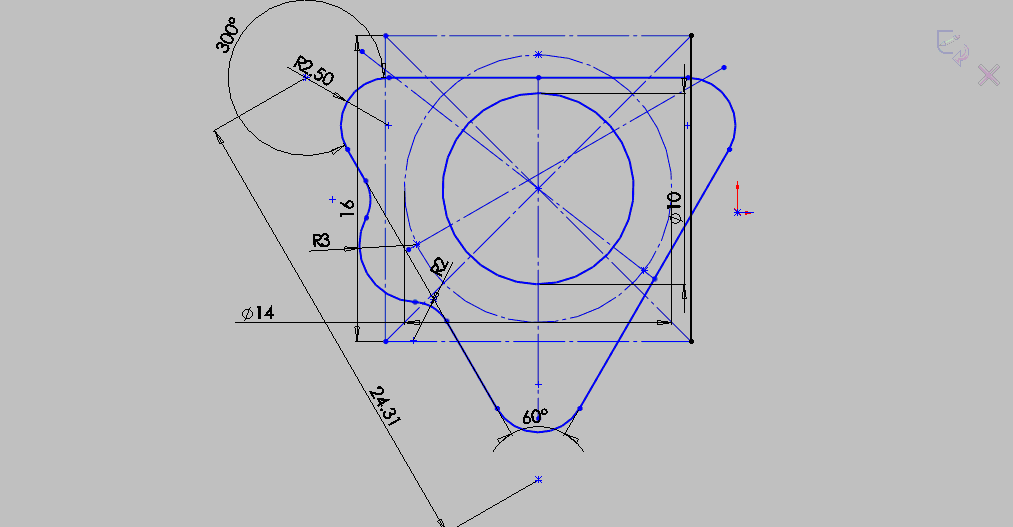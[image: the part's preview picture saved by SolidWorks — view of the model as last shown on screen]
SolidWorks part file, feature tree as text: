
SOLIDWORKS PART (.sldprt)
format: sldprt  version: not decoded by parser v0  size: 189,952 bytes
history: native  units: mm
features: sketch x5, cut_extrude x2, material x1, extrude x1, pattern_circular x1, hole x1 (+14 scaffold rows collapsed)
feature tree (25):
  scaffold x14  (default folders/planes/origin — collapsed)
  material  "Material <not specified>"
  sketch  "Sketch1"  dims[c1.D1=2.5mm c1.D5=1.0mm c2.D1=10.0mm c2.D6=2.5mm c2.D5=14.0mm c2.D7=3.0mm c2.D8=2.0mm c2.D2=~14.352682mm c3.D2=300.0deg c3.D3=~13.069491mm c4.D3=60.0deg c4.D4=~7.545674mm c5.D4=60.0deg c6.D4=24.31mm c6.D6=~8.917862mm c6.D7=~9.953438mm c6.D8=10.0mm c7.D6=10.0mm c7.D9=~11.012771mm c8.D9=90.0deg c9.D9=16.0mm c9.D10=12.0mm]
  extrude  "Extrude1"  Depth=4mm
  sketch  "Sketch2"  dims[c1.D1=6.35mm c1.D3=4.7625mm c1.D2=~1.903355mm c2.D2=45.0deg c2.D1=3.175mm]
  cut_extrude  "Extrude2"  [1 undecoded]
  pattern_circular  "CirPattern1"  Count=3 Angle=360deg
  hole  "M3 Clearance Hole1"  Diameter=3.4mm Depth=10mm
  sketch  "3DSketch1"
  sketch  "Sketch6"  dims[hole-wizard template sketch: 50 standard entries collapsed; hole parameters above]
  cut_extrude  "Extrude3"  [1 undecoded]
  sketch  "Sketch2<3>"  dims[D1=9.0mm BallDiameter=10.0mm]
decode coverage: 7 of 10 modeling features carry decoded parameters
note: ~ marks probable driven/reference dimensions
note: 2 parameter values undecoded
note: suppression state not decoded; provenance and decode notes live in map.json
